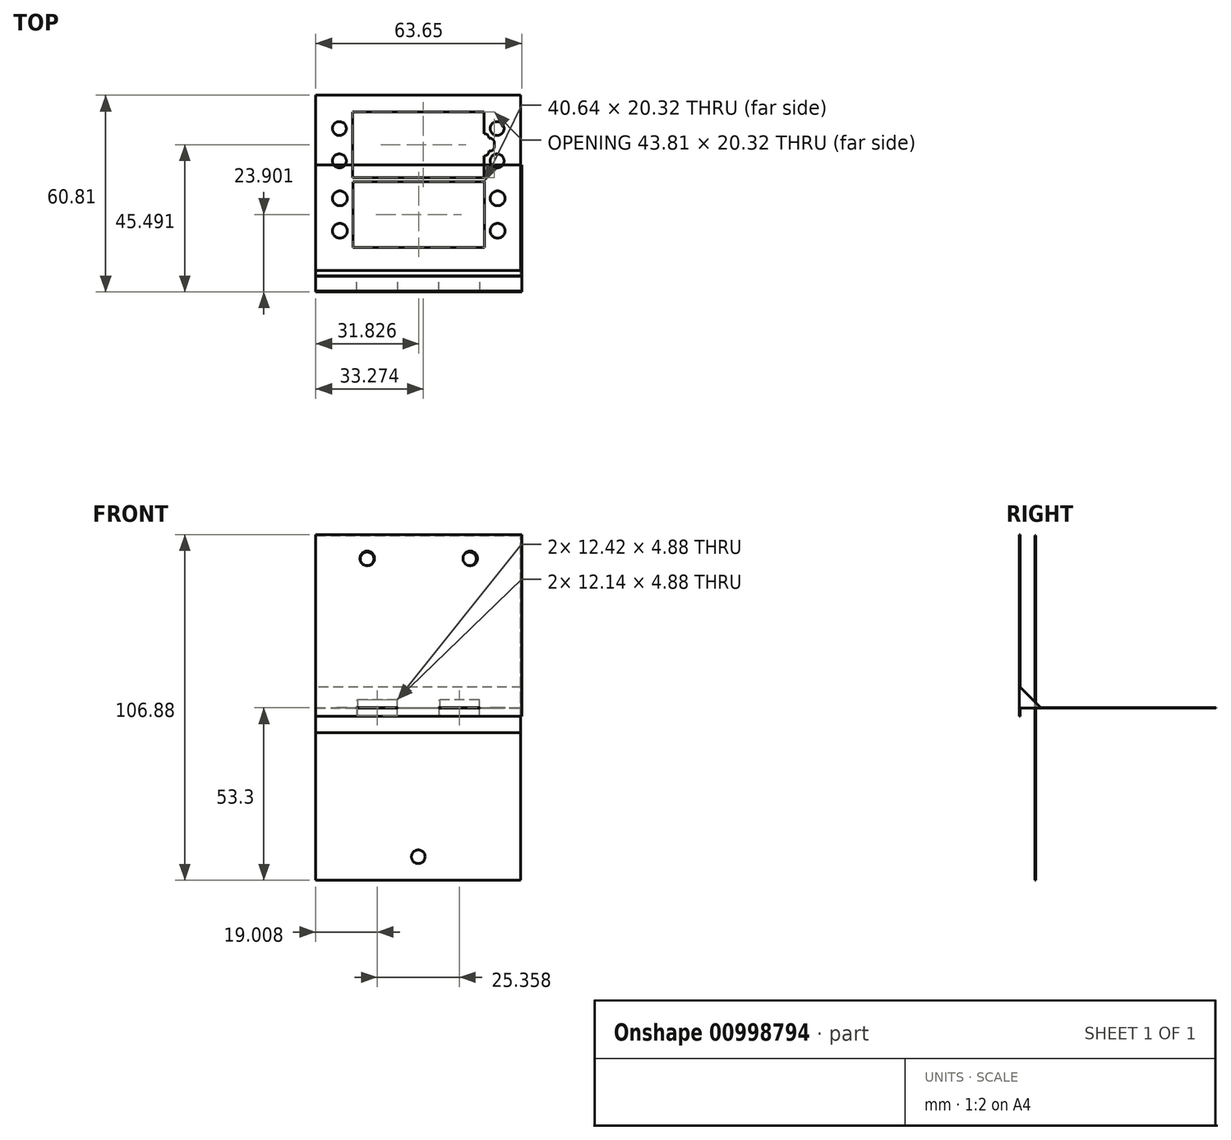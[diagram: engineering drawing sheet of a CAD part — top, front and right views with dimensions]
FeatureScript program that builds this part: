
annotation { "Feature Type Name" : "Feature", "Feature Type Description" : "" }
export const myFeature = defineFeature(function(context is Context, id is Id, definition is map)
    precondition{}
    {
        {
            assignVariable(context, id + "F0", {"name" : "absThickness", "anyValue" : .203});
        }
        {
            var Q0;
            Q0=qCreatedBy(makeId("Top.planeOp"),FACE);
            var sketch = newSketch(context, id + "F1", { "sketchPlane" : qUnion([Q0])});
            skLineSegment(sketch, "E0.top", {"start": v(0, 39.22) * mm, "end": v(63.65, 39.22) * mm});
            skLineSegment(sketch, "E0.left", {"start": v(0, 0) * mm, "end": v(0, 39.22) * mm});
            skLineSegment(sketch, "E0.right", {"start": v(63.65, 0) * mm, "end": v(63.65, 39.22) * mm});
            skLineSegment(sketch, "E1.bottom", {"start": v(11.5, 34.06) * mm, "end": v(52.15, 34.06) * mm});
            skLineSegment(sketch, "E1.top", {"start": v(11.5, 13.74) * mm, "end": v(52.15, 13.74) * mm});
            skLineSegment(sketch, "E1.left", {"start": v(11.5, 34.06) * mm, "end": v(11.5, 13.74) * mm});
            skLineSegment(sketch, "E1.right", {"start": v(52.15, 34.06) * mm, "end": v(52.15, 13.74) * mm});
            skCircle(sketch, "E2", {"center": v(7.44, 28.9) * mm, "radius": 2.29 * mm});
            skCircle(sketch, "E3", {"center": v(7.44, 18.9) * mm, "radius": 2.29 * mm});
            skCircle(sketch, "E4", {"center": v(56.21, 18.9) * mm, "radius": 2.29 * mm});
            skCircle(sketch, "E5", {"center": v(56.21, 28.9) * mm, "radius": 2.29 * mm});
            skLineSegment(sketch, "E6", {"start": v(7.44, 28.9) * mm, "end": v(7.44, 18.9) * mm, "construction": true});
            skLineSegment(sketch, "E7", {"start": v(56.21, 28.9) * mm, "end": v(56.21, 18.9) * mm, "construction": true});
            skLineSegment(sketch, "E8", {"start": v(7.44, 23.9) * mm, "end": v(11.5, 23.9) * mm, "construction": true});
            skLineSegment(sketch, "E9", {"start": v(56.21, 23.9) * mm, "end": v(52.15, 23.9) * mm, "construction": true});
            skLineSegment(sketch, "E10", {"start": v(31.83, 34.06) * mm, "end": v(31.83, 39.22) * mm, "construction": true});
            skLineSegment(sketch, "E11", {"start": v(5.16, 28.9) * mm, "end": v(0, 28.9) * mm, "construction": true});
            skLineSegment(sketch, "E12", {"start": v(11.5, 23.9) * mm, "end": v(11.5, 0) * mm, "construction": true});
            skLineSegment(sketch, "E13", {"start": v(0, 0) * mm, "end": v(63.65, 0) * mm});
            skSolve(sketch);
        }
        {
            var Q0;
            Q0 = qSketchRegion(id + "F1", true);
            extrude(context, id + "F2", {"entities" : qUnion([Q0]), "endBound" : BoundingType.SYMMETRIC, "depth" : (getVariable(context, 'absThickness')) * mm, "offsetDistance" : 25.4 * mm});
        }
        {
            var Q0;
            Q0=qCreatedBy(makeId("Front.planeOp"),FACE);
            var sketch = newSketch(context, id + "F3", { "sketchPlane" : qUnion([Q0])});
            skLineSegment(sketch, "E14.bottom", {"start": v(0, -2.58) * mm, "end": v(63.65, -2.58) * mm});
            skLineSegment(sketch, "E14.top", {"start": v(0, 53.58) * mm, "end": v(63.65, 53.58) * mm});
            skLineSegment(sketch, "E14.left", {"start": v(0, -2.58) * mm, "end": v(0, 53.58) * mm});
            skLineSegment(sketch, "E14.right", {"start": v(63.65, -2.58) * mm, "end": v(63.65, 53.58) * mm});
            skCircle(sketch, "E15", {"center": v(15.91, 46.18) * mm, "radius": 2.25 * mm});
            skCircle(sketch, "E16", {"center": v(47.74, 46.18) * mm, "radius": 2.25 * mm});
            skLineSegment(sketch, "E17", {"start": v(15.91, 46.18) * mm, "end": v(0, 46.18) * mm, "construction": true});
            skLineSegment(sketch, "E18", {"start": v(47.74, 46.18) * mm, "end": v(63.65, 46.18) * mm, "construction": true});
            skLineSegment(sketch, "E19", {"start": v(15.91, 46.18) * mm, "end": v(31.83, 46.18) * mm, "construction": true});
            skLineSegment(sketch, "E20", {"start": v(31.83, 46.18) * mm, "end": v(47.74, 46.18) * mm, "construction": true});
            skLineSegment(sketch, "E21", {"start": v(15.91, 48.43) * mm, "end": v(15.91, 53.58) * mm, "construction": true});
            skLineSegment(sketch, "E22", {"start": v(0, 38.77) * mm, "end": v(63.65, 38.77) * mm, "construction": true});
            skLineSegment(sketch, "E23", {"start": v(15.91, 43.93) * mm, "end": v(15.91, 38.77) * mm, "construction": true});
            skSolve(sketch);
        }
        {
            var Q0;
            Q0 = qSketchRegion(id + "F3", true);
            extrude(context, id + "F4", {"entities" : qUnion([Q0]), "operationType" : NewBodyOperationType.ADD, "oppositeDirection" : true, "depth" : (getVariable(context, 'absThickness')) * mm, "offsetDistance" : 25.4 * mm});
        }
        {
            var Q0;
            Q0=makeQuery(id+"F4.boolean.opBoolean","INTERSECT",EDGE,{"derivedFrom":[makeQuery(id+"F2.opExtrude","CAP_FACE",FACE,{"disambiguationData":[OSD([sQuery(id+"F1.wireOp",EDGE,"E0.top"),sQuery(id+"F1.wireOp",EDGE,"E0.left"),sQuery(id+"F1.wireOp",EDGE,"E0.right"),sQuery(id+"F1.wireOp",EDGE,"E1.bottom"),sQuery(id+"F1.wireOp",EDGE,"E1.top"),sQuery(id+"F1.wireOp",EDGE,"E1.left"),sQuery(id+"F1.wireOp",EDGE,"E1.right"),sQuery(id+"F1.wireOp",EDGE,"E2"),sQuery(id+"F1.wireOp",EDGE,"E3"),sQuery(id+"F1.wireOp",EDGE,"E4"),sQuery(id+"F1.wireOp",EDGE,"E5"),sQuery(id+"F1.wireOp",EDGE,"E13")])],"isStart":false}),makeQuery(id+"F4.opExtrude","CAP_FACE",FACE,{"disambiguationData":[OSD([sQuery(id+"F3.wireOp",EDGE,"E14.bottom"),sQuery(id+"F3.wireOp",EDGE,"E14.top"),sQuery(id+"F3.wireOp",EDGE,"E14.left"),sQuery(id+"F3.wireOp",EDGE,"E14.right"),sQuery(id+"F3.wireOp",EDGE,"E15"),sQuery(id+"F3.wireOp",EDGE,"E16")])],"isStart":false})]});
            chamfer(context, id + "F5", {"entities" : qUnion([Q0]), "width" : 6.35 * mm, "tangentPropagation" : true});
        }
        {
            var Q0;
            Q0=qCreatedBy(makeId("Top.planeOp"),FACE);
            var sketch = newSketch(context, id + "F6", { "sketchPlane" : qUnion([Q0])});
            skLineSegment(sketch, "E24.top", {"start": v(0, 60.8) * mm, "end": v(63.37, 60.8) * mm});
            skLineSegment(sketch, "E24.left", {"start": v(0, 0) * mm, "end": v(0, 60.8) * mm, "construction": true});
            skLineSegment(sketch, "E24.right", {"start": v(63.37, 0) * mm, "end": v(63.37, 60.8) * mm, "construction": true});
            skLineSegment(sketch, "E25.bottom", {"start": v(11.37, 55.65) * mm, "end": v(52, 55.65) * mm});
            skLineSegment(sketch, "E25.top", {"start": v(11.37, 35.33) * mm, "end": v(52, 35.33) * mm});
            skLineSegment(sketch, "E25.left", {"start": v(11.37, 55.65) * mm, "end": v(11.37, 35.33) * mm});
            skLineSegment(sketch, "E25.right", {"start": v(52, 55.65) * mm, "end": v(52, 35.33) * mm, "construction": true});
            skCircle(sketch, "E26", {"center": v(7.3, 50.5) * mm, "radius": 2.15 * mm});
            skCircle(sketch, "E27", {"center": v(7.3, 40.49) * mm, "radius": 2.15 * mm});
            skCircle(sketch, "E28", {"center": v(56.07, 40.49) * mm, "radius": 2.15 * mm});
            skCircle(sketch, "E29", {"center": v(56.07, 50.5) * mm, "radius": 2.15 * mm});
            skLineSegment(sketch, "E30", {"start": v(7.3, 50.5) * mm, "end": v(7.3, 40.49) * mm, "construction": true});
            skLineSegment(sketch, "E31", {"start": v(56.07, 50.5) * mm, "end": v(56.07, 40.49) * mm, "construction": true});
            skLineSegment(sketch, "E32", {"start": v(7.3, 45.5) * mm, "end": v(11.37, 45.5) * mm, "construction": true});
            skLineSegment(sketch, "E33", {"start": v(56.07, 45.5) * mm, "end": v(52, 45.5) * mm, "construction": true});
            skLineSegment(sketch, "E34", {"start": v(31.69, 55.65) * mm, "end": v(31.69, 60.8) * mm, "construction": true});
            skLineSegment(sketch, "E35", {"start": v(5.16, 50.5) * mm, "end": v(0, 50.5) * mm, "construction": true});
            skLineSegment(sketch, "E36", {"start": v(11.37, 45.5) * mm, "end": v(11.37, 0) * mm, "construction": true});
            skLineSegment(sketch, "E37", {"start": v(0, 0) * mm, "end": v(63.37, 0) * mm, "construction": true});
            skLineSegment(sketch, "E38.bottom", {"start": v(12.66, 0) * mm, "end": v(25.36, 0) * mm});
            skLineSegment(sketch, "E38.top", {"start": v(12.66, 5.02) * mm, "end": v(25.36, 5.02) * mm, "construction": true});
            skLineSegment(sketch, "E38.left", {"start": v(12.66, 0) * mm, "end": v(12.66, 5.02) * mm});
            skLineSegment(sketch, "E38.right", {"start": v(25.36, 0) * mm, "end": v(25.36, 5.02) * mm});
            skLineSegment(sketch, "E39.bottom", {"start": v(38.02, 0) * mm, "end": v(50.72, 0) * mm});
            skLineSegment(sketch, "E39.top", {"start": v(38.02, 5.02) * mm, "end": v(50.72, 5.02) * mm, "construction": true});
            skLineSegment(sketch, "E39.left", {"start": v(38.02, 0) * mm, "end": v(38.02, 5.02) * mm});
            skLineSegment(sketch, "E39.right", {"start": v(50.72, 0) * mm, "end": v(50.72, 5.02) * mm});
            skLineSegment(sketch, "E40", {"start": v(0, 5.02) * mm, "end": v(12.66, 5.02) * mm});
            skLineSegment(sketch, "E41", {"start": v(25.36, 5.02) * mm, "end": v(38.02, 5.02) * mm});
            skLineSegment(sketch, "E42", {"start": v(50.72, 5.02) * mm, "end": v(63.37, 5.02) * mm});
            skLineSegment(sketch, "E43", {"start": v(0, 5.02) * mm, "end": v(0, 60.8) * mm});
            skLineSegment(sketch, "E44", {"start": v(63.37, 5.02) * mm, "end": v(63.37, 60.8) * mm});
            skLineSegment(sketch, "E45.bottom", {"start": v(52, 48.92) * mm, "end": v(52.07, 48.92) * mm});
            skLineSegment(sketch, "E45.top", {"start": v(52, 42.06) * mm, "end": v(52.07, 42.06) * mm});
            skLineSegment(sketch, "E45.left", {"start": v(52, 48.92) * mm, "end": v(52, 42.06) * mm, "construction": true});
            skLineSegment(sketch, "E45.right", {"start": v(53.53, 47.46) * mm, "end": v(53.53, 43.52) * mm, "construction": true});
            skPoint(sketch, "E46.visualSharp", {"position": v(53.53, 48.92) * mm});
            skArc(sketch, "E46.filletArc", {"start": v(53.53, 47.46) * mm, "mid": v(53.1, 48.5) * mm, "end": v(52.07, 48.92) * mm});
            skPoint(sketch, "E47.visualSharp", {"position": v(53.53, 42.06) * mm});
            skArc(sketch, "E47.filletArc", {"start": v(52.07, 42.06) * mm, "mid": v(53.1, 42.5) * mm, "end": v(53.53, 43.52) * mm});
            skLineSegment(sketch, "E48.bottom", {"start": v(53.53, 47.46) * mm, "end": v(55.18, 47.46) * mm});
            skLineSegment(sketch, "E48.top", {"start": v(53.53, 43.52) * mm, "end": v(55.18, 43.52) * mm});
            skLineSegment(sketch, "E48.right", {"start": v(55.18, 47.46) * mm, "end": v(55.18, 43.52) * mm});
            skLineSegment(sketch, "E49", {"start": v(53.53, 45.5) * mm, "end": v(52, 45.5) * mm, "construction": true});
            skLineSegment(sketch, "E50", {"start": v(52, 42.06) * mm, "end": v(52, 35.33) * mm});
            skLineSegment(sketch, "E51", {"start": v(52, 48.92) * mm, "end": v(52, 55.65) * mm});
            skSolve(sketch);
        }
        {
            var Q0;
            Q0 = qSketchRegion(id + "F6", true);
            extrude(context, id + "F7", {"entities" : qUnion([Q0]), "endBound" : BoundingType.SYMMETRIC, "depth" : (getVariable(context, 'absThickness')) * mm, "offsetDistance" : 25.4 * mm});
        }
        {
            var Q0;
            Q0=makeQuery(id+"F7.opExtrude","SWEPT_FACE",FACE,{"disambiguationData":[OSD([sQuery(id+"F6.wireOp",EDGE,"E40")])]});
            var sketch = newSketch(context, id + "F8", { "sketchPlane" : qUnion([Q0])});
            skLineSegment(sketch, "E52.bottom", {"start": v(0, -7.73) * mm, "end": v(63.37, -7.73) * mm});
            skLineSegment(sketch, "E52.top", {"start": v(0, 53.3) * mm, "end": v(63.37, 53.3) * mm});
            skLineSegment(sketch, "E52.left", {"start": v(0, -7.73) * mm, "end": v(0, 53.3) * mm});
            skLineSegment(sketch, "E52.right", {"start": v(63.37, -7.73) * mm, "end": v(63.37, 53.3) * mm});
            skCircle(sketch, "E53", {"center": v(15.84, 46.04) * mm, "radius": 2.1 * mm});
            skCircle(sketch, "E54", {"center": v(47.53, 46.04) * mm, "radius": 2.1 * mm});
            skLineSegment(sketch, "E55", {"start": v(15.84, 46.04) * mm, "end": v(0, 46.04) * mm, "construction": true});
            skLineSegment(sketch, "E56", {"start": v(47.53, 46.04) * mm, "end": v(63.37, 46.04) * mm, "construction": true});
            skLineSegment(sketch, "E57", {"start": v(15.84, 46.04) * mm, "end": v(31.69, 46.04) * mm, "construction": true});
            skLineSegment(sketch, "E58", {"start": v(31.69, 46.04) * mm, "end": v(47.53, 46.04) * mm, "construction": true});
            skLineSegment(sketch, "E59", {"start": v(15.84, 48.15) * mm, "end": v(15.84, 53.3) * mm, "construction": true});
            skLineSegment(sketch, "E60", {"start": v(0, 38.77) * mm, "end": v(63.37, 38.77) * mm, "construction": true});
            skLineSegment(sketch, "E61", {"start": v(15.84, 43.93) * mm, "end": v(15.84, 38.77) * mm, "construction": true});
            skLineSegment(sketch, "E62", {"start": v(50.72, 2.58) * mm, "end": v(38.02, -2.58) * mm, "construction": true});
            skLineSegment(sketch, "E63", {"start": v(25.36, 2.58) * mm, "end": v(12.66, -2.58) * mm, "construction": true});
            skLineSegment(sketch, "E64.bottom", {"start": v(50.58, -2.44) * mm, "end": v(38.16, -2.44) * mm});
            skLineSegment(sketch, "E64.top", {"start": v(50.58, 2.44) * mm, "end": v(38.16, 2.44) * mm});
            skLineSegment(sketch, "E64.left", {"start": v(50.58, -2.44) * mm, "end": v(50.58, 2.44) * mm});
            skLineSegment(sketch, "E64.right", {"start": v(38.16, -2.44) * mm, "end": v(38.16, 2.44) * mm});
            skPoint(sketch, "E64.middle", {"position": v(44.37, 0) * mm});
            skLineSegment(sketch, "E65.bottom", {"start": v(25.22, -2.44) * mm, "end": v(12.8, -2.44) * mm});
            skLineSegment(sketch, "E65.top", {"start": v(25.22, 2.44) * mm, "end": v(12.8, 2.44) * mm});
            skLineSegment(sketch, "E65.left", {"start": v(25.22, -2.44) * mm, "end": v(25.22, 2.44) * mm});
            skLineSegment(sketch, "E65.right", {"start": v(12.8, -2.44) * mm, "end": v(12.8, 2.44) * mm});
            skPoint(sketch, "E65.middle", {"position": v(19, 0) * mm});
            skSolve(sketch);
        }
        {
            var Q0;
            Q0 = qSketchRegion(id + "F8", true);
            extrude(context, id + "F9", {"entities" : qUnion([Q0]), "depth" : (getVariable(context, 'absThickness')) * mm, "offsetDistance" : 25.4 * mm});
        }
        {
            var Q0;
            Q0=makeQuery(id+"F7.opExtrude","SWEPT_EDGE",EDGE,{"disambiguationData":[OSD([sQuery(id+"F6.wireOp",EDGE,"E48.bottom"),sQuery(id+"F6.wireOp",EDGE,"E48.right")])]});
            var Q1;
            Q1=makeQuery(id+"F7.opExtrude","SWEPT_EDGE",EDGE,{"disambiguationData":[OSD([sQuery(id+"F6.wireOp",EDGE,"E48.top"),sQuery(id+"F6.wireOp",EDGE,"E48.right")])]});
            fillet(context, id + "F10", {"entities" : qUnion([Q0, Q1]), "radius" : 1.27 * mm, "tangentPropagation" : true, "allowEdgeOverflow" : false});
        }
        {
            var Q0;
            Q0=makeQuery(id+"F7.opExtrude","SWEPT_FACE",FACE,{"disambiguationData":[OSD([sQuery(id+"F6.wireOp",EDGE,"E40")])]});
            var sketch = newSketch(context, id + "F11", { "sketchPlane" : qUnion([Q0])});
            skLineSegment(sketch, "E66.bottom", {"start": v(0, 53.3) * mm, "end": v(63.37, 53.3) * mm});
            skLineSegment(sketch, "E66.top", {"start": v(0, -53.3) * mm, "end": v(63.37, -53.3) * mm});
            skLineSegment(sketch, "E66.left", {"start": v(0, 53.3) * mm, "end": v(0, -53.3) * mm});
            skLineSegment(sketch, "E66.right", {"start": v(63.37, 53.3) * mm, "end": v(63.37, -53.3) * mm});
            skLineSegment(sketch, "E67", {"start": v(12.66, 2.58) * mm, "end": v(25.36, -2.58) * mm, "construction": true});
            skLineSegment(sketch, "E68", {"start": v(38.02, 2.58) * mm, "end": v(50.72, -2.58) * mm, "construction": true});
            skLineSegment(sketch, "E69.bottom", {"start": v(25.08, 2.44) * mm, "end": v(12.94, 2.44) * mm});
            skLineSegment(sketch, "E69.top", {"start": v(25.08, -2.44) * mm, "end": v(12.94, -2.44) * mm});
            skLineSegment(sketch, "E69.left", {"start": v(25.08, 2.44) * mm, "end": v(25.08, -2.44) * mm});
            skLineSegment(sketch, "E69.right", {"start": v(12.94, 2.44) * mm, "end": v(12.94, -2.44) * mm});
            skPoint(sketch, "E69.middle", {"position": v(19, 0) * mm});
            skLineSegment(sketch, "E70.bottom", {"start": v(50.44, 2.44) * mm, "end": v(38.3, 2.44) * mm});
            skLineSegment(sketch, "E70.top", {"start": v(50.44, -2.44) * mm, "end": v(38.3, -2.44) * mm});
            skLineSegment(sketch, "E70.left", {"start": v(50.44, 2.44) * mm, "end": v(50.44, -2.44) * mm});
            skLineSegment(sketch, "E70.right", {"start": v(38.3, 2.44) * mm, "end": v(38.3, -2.44) * mm});
            skPoint(sketch, "E70.middle", {"position": v(44.37, 0) * mm});
            skCircle(sketch, "E71", {"center": v(15.84, 46.04) * mm, "radius": 2.1 * mm});
            skCircle(sketch, "E72", {"center": v(47.53, 46.04) * mm, "radius": 2.1 * mm});
            skLineSegment(sketch, "E73", {"start": v(15.84, 46.04) * mm, "end": v(47.53, 46.04) * mm, "construction": true});
            skLineSegment(sketch, "E74", {"start": v(31.69, 53.3) * mm, "end": v(31.69, 46.04) * mm, "construction": true});
            skLineSegment(sketch, "E75", {"start": v(44.37, 0) * mm, "end": v(44.37, 53.3) * mm, "construction": true});
            skLineSegment(sketch, "E76", {"start": v(44.37, 0) * mm, "end": v(44.37, -53.3) * mm, "construction": true});
            skCircle(sketch, "E77", {"center": v(31.69, -46.04) * mm, "radius": 2.1 * mm});
            skLineSegment(sketch, "E78", {"start": v(31.69, -46.04) * mm, "end": v(31.69, -53.3) * mm, "construction": true});
            skSolve(sketch);
        }
        {
            var Q0;
            Q0 = qSketchRegion(id + "F11", true);
            extrude(context, id + "F12", {"entities" : qUnion([Q0]), "depth" : (getVariable(context, 'absThickness')) * mm, "offsetDistance" : 25.4 * mm});
        }
    });
